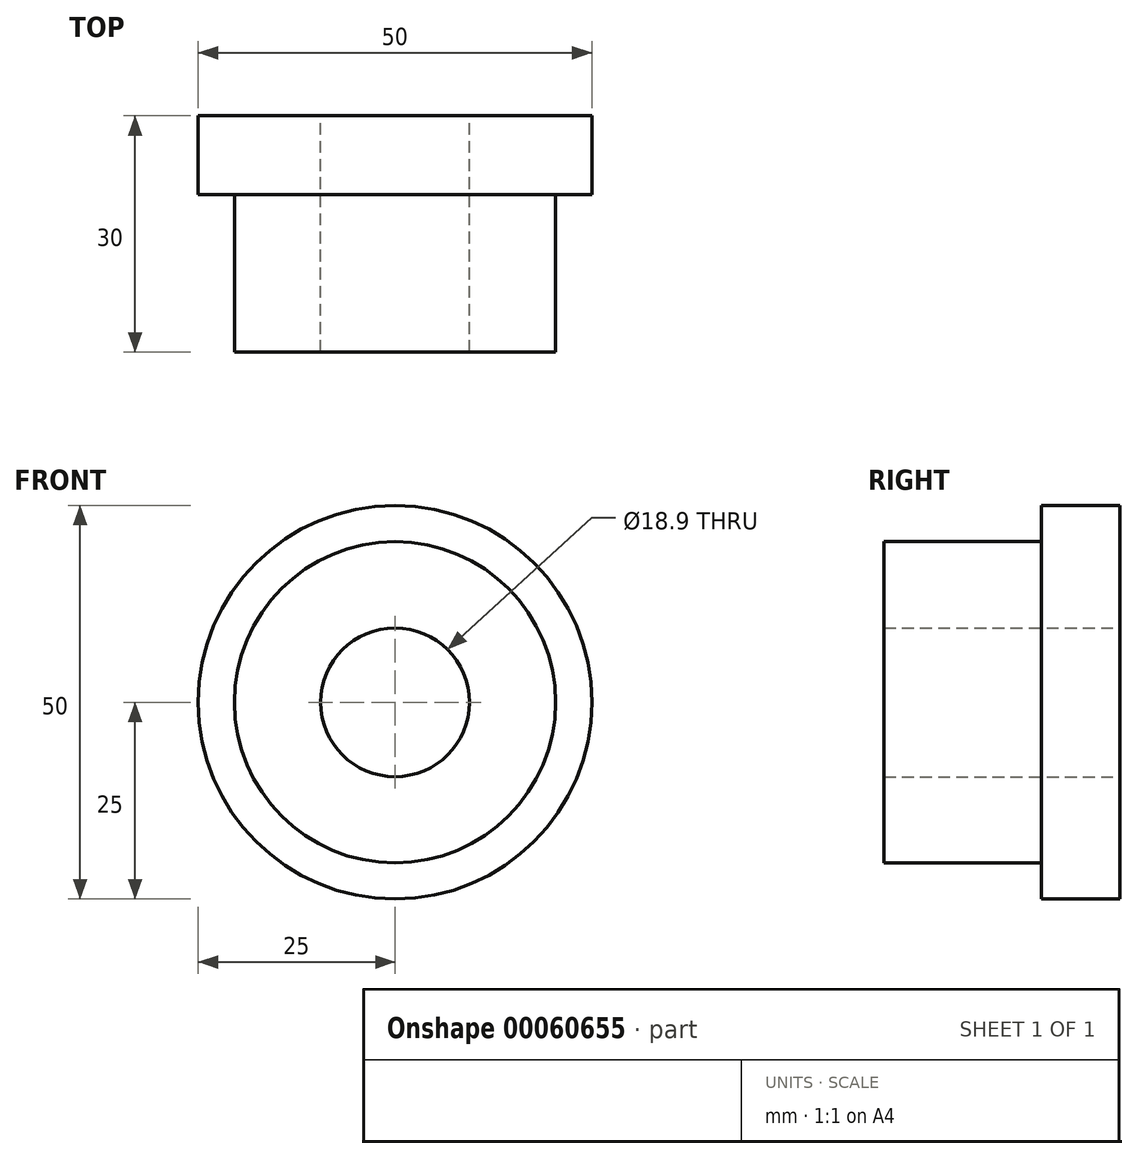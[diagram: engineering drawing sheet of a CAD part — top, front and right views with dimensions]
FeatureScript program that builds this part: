
annotation { "Feature Type Name" : "Feature", "Feature Type Description" : "" }
export const myFeature = defineFeature(function(context is Context, id is Id, definition is map)
    precondition{}
    {
        {
            var Q0;
            Q0=qCreatedBy(makeId("Front.planeOp"),FACE);
            var sketch = newSketch(context, id + "F0", { "sketchPlane" : qUnion([Q0])});
            skCircle(sketch, "E0", {"center": v(0, 0) * mm, "radius": 9.45 * mm});
            skCircle(sketch, "E1", {"center": v(0, 0) * mm, "radius": 25 * mm});
            skCircle(sketch, "E2", {"center": v(0, 0) * mm, "radius": 20.4 * mm});
            skSolve(sketch);
        }
        {
            var Q0;
            Q0=makeQuery(id+"F0.imprint","IMPRINT",FACE,{"disambiguationData":[TD([[makeQuery(id+"F0.imprint","IMPRINT",EDGE,{"derivedFrom":sQuery(id+"F0.wireOp",EDGE,"E0")}),-1.0]])]});
            extrude(context, id + "F1", {"entities" : qUnion([Q0]), "depth" : 30 * mm});
        }
        {
            var Q0;
            Q0 = qSketchRegion(id + "F0", true);
            extrude(context, id + "F2", {"entities" : qUnion([Q0]), "operationType" : NewBodyOperationType.ADD, "depth" : 10 * mm});
        }
    });
